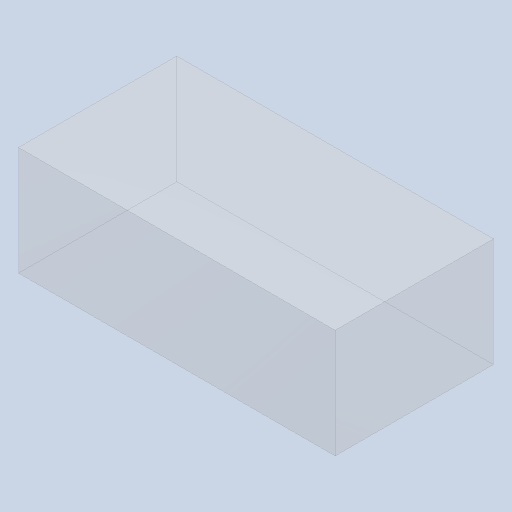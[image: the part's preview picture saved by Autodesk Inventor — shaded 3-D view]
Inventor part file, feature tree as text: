
AUTODESK INVENTOR PART (.ipt)
format: ipt  version: 2022.1 (Build 261234000, 234)  size: 88,576 bytes
history: imported  units: mm
features: imported_body x1
ambient origin geometry x8: Origin, YZ Plane, XZ Plane, XY Plane, X Axis, Y Axis, Z Axis, Center Point
bodies: Solid1 (imported_parasolid)
feature tree (1):
  imported_body  NMx_Import_Brep_tag  [imported B-rep: ~6 faces, bbox_mm=[1.6, 0.55, 0.8]]
